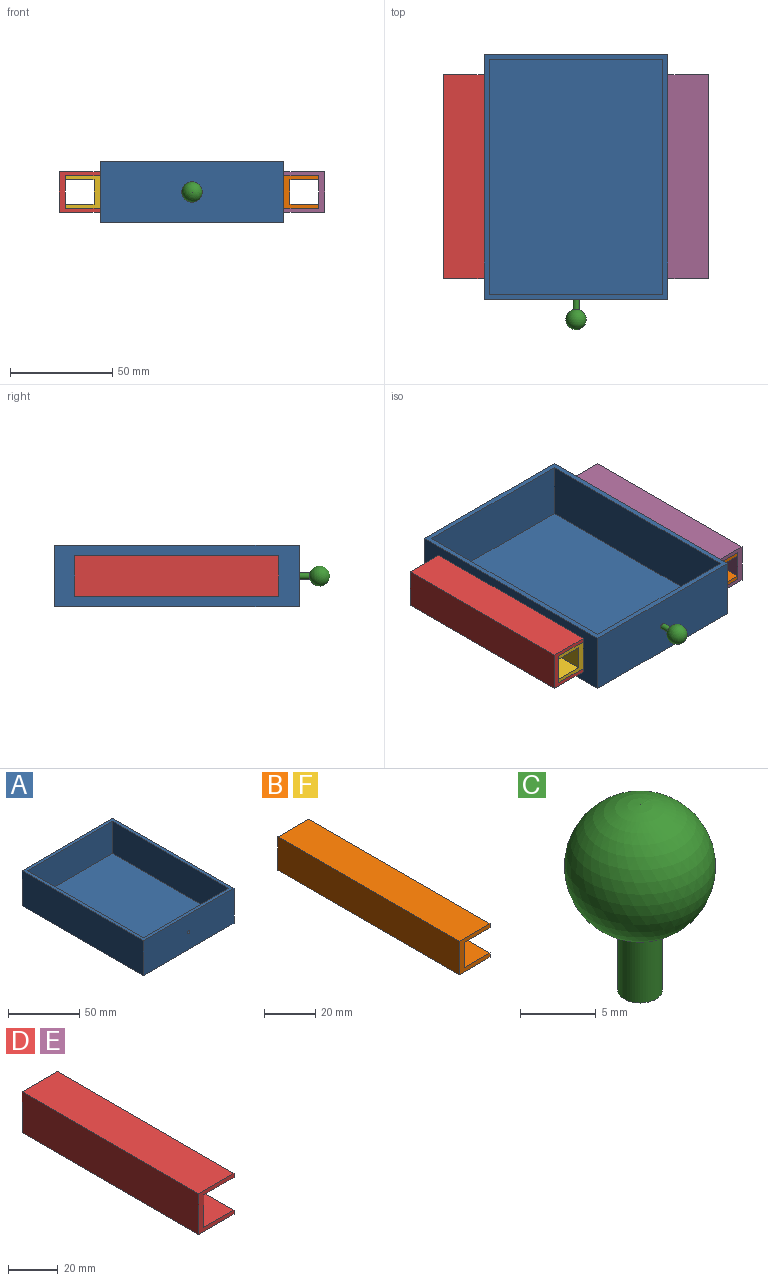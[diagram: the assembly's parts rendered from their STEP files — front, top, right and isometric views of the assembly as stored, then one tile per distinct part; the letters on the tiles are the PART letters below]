
ASSEMBLY  parts=6 mates=5
PART A: 12 faces, bbox 90x120x30 mm
  f0: plane 120x90mm, normal (0,0,1), area 1025mm2, adj f1,f3,f4,f5,f6,f8,f9,f10
  f1: plane 120x30mm, normal (-1,0,0), area 3600mm2, adj f0,f2,f4,f5
  f2: plane 120x90mm, normal (0,0,-1), area 10800mm2, adj f1,f3,f4,f5
  f3: plane 120x30mm, normal (1,0,0), area 3600mm2, adj f0,f2,f4,f5
  f4: plane 90x30mm, normal (0,-1,0), area 2695.1mm2, adj f0,f1,f2,f3,f11
  f5: plane 90x30mm, normal (0,1,0), area 2700mm2, adj f0,f1,f2,f3
  f6: plane 115x27.5mm, normal (1,0,0), area 3162.5mm2, adj f0,f7,f9,f10
  f7: plane 115x85mm, normal (0,0,1), area 9775mm2, adj f6,f8,f9,f10
  f8: plane 115x27.5mm, normal (-1,0,0), area 3162.5mm2, adj f0,f7,f9,f10
  f9: plane 85x27.5mm, normal (0,1,0), area 2332.6mm2, adj f0,f6,f7,f8,f11
  f10: plane 85x27.5mm, normal (0,-1,0), area 2337.5mm2, adj f0,f6,f7,f8
  f11: cylinder r=1.25mm len=2.5mm, axis (0,-1,0), area 19.6mm2, adj f4,f9
PART B: 10 faces, bbox 17x100x16 mm
  f0: plane 100x17mm, normal (0,0,-1), area 1700mm2, adj f1,f7,f8,f9
  f1: plane 100x2mm, normal (1,0,0), area 200mm2, adj f0,f2,f8,f9
  f2: plane 100x14mm, normal (0,0,1), area 1400mm2, adj f1,f3,f8,f9
  f3: plane 100x12mm, normal (1,0,0), area 1200mm2, adj f2,f4,f8,f9
  f4: plane 100x14mm, normal (0,0,-1), area 1400mm2, adj f3,f5,f8,f9
  f5: plane 100x2mm, normal (1,0,0), area 200mm2, adj f4,f6,f8,f9
  f6: plane 100x17mm, normal (0,0,1), area 1700mm2, adj f5,f7,f8,f9
  f7: plane 100x16mm, normal (-1,0,0), area 1600mm2, adj f0,f6,f8,f9
  f8: plane 17x16mm, normal (0,-1,0), area 104mm2, adj f0,f1,f2,f3,f4,f5,f6,f7
  f9: plane 17x16mm, normal (0,1,0), area 104mm2, adj f0,f1,f2,f3,f4,f5,f6,f7
PART C: 3 faces, bbox 10x10x15 mm
  f0: plane 2.96x2.96mm, normal (0,0,-1), area 6.9mm2, adj f1
  f1: cylinder r=1.48mm len=5.22mm, axis (0,0,1), area 48.5mm2, adj f0,f2
  f2: sphere r=5mm, area 307.1mm2, adj f1
PART D: 10 faces, bbox 20x100x20 mm
  f0: plane 100x20mm, normal (0,0,-1), area 2000mm2, adj f1,f7,f8,f9
  f1: plane 100x2mm, normal (1,0,0), area 200mm2, adj f0,f2,f8,f9
  f2: plane 100x17mm, normal (0,0,1), area 1700mm2, adj f1,f3,f8,f9
  f3: plane 100x16mm, normal (1,0,0), area 1600mm2, adj f2,f4,f8,f9
  f4: plane 100x17mm, normal (0,0,-1), area 1700mm2, adj f3,f5,f8,f9
  f5: plane 100x2mm, normal (1,0,0), area 200mm2, adj f4,f6,f8,f9
  f6: plane 100x20mm, normal (0,0,1), area 2000mm2, adj f5,f7,f8,f9
  f7: plane 100x20mm, normal (-1,0,0), area 2000mm2, adj f0,f6,f8,f9
  f8: plane 20x20mm, normal (0,-1,0), area 128mm2, adj f0,f1,f2,f3,f4,f5,f6,f7
  f9: plane 20x20mm, normal (0,1,0), area 128mm2, adj f0,f1,f2,f3,f4,f5,f6,f7
PART E: same geometry as D
PART F: same geometry as B
PLACE A t=(-52.6,-1.52,-8.63)mm
PLACE B t=(0.9,-11.52,-8.63)mm
PLACE C rot(axis=(1,0,0),90deg) t=(-52.6,-131.52,-8.63)mm
PLACE D t=(-107.6,-11.52,-8.63)mm fixed
PLACE E rot(axis=(0,0,1),180deg) t=(2.4,-111.52,-8.63)mm
PLACE F rot(axis=(0,-1,0),180deg) t=(-106.1,-11.52,-8.63)mm
MATE fastened F.f7 <-> A.f1  axis (1,0,0) through (-97.6,-61.52,-8.63)mm
MATE fastened C.f1 <-> A.f11  axis (0,1,0) through (-52.6,-121.52,-8.63)mm
MATE planar E.f4 <-> B.f6  axis (0,0,-1) through (0.9,-61.52,-0.63)mm
MATE fastened B.f7 <-> A.f3  axis (-1,0,0) through (-7.6,-61.52,-8.63)mm
MATE planar F.f0 <-> D.f4  axis (0,0,1) through (-106.1,-61.52,-0.63)mm
